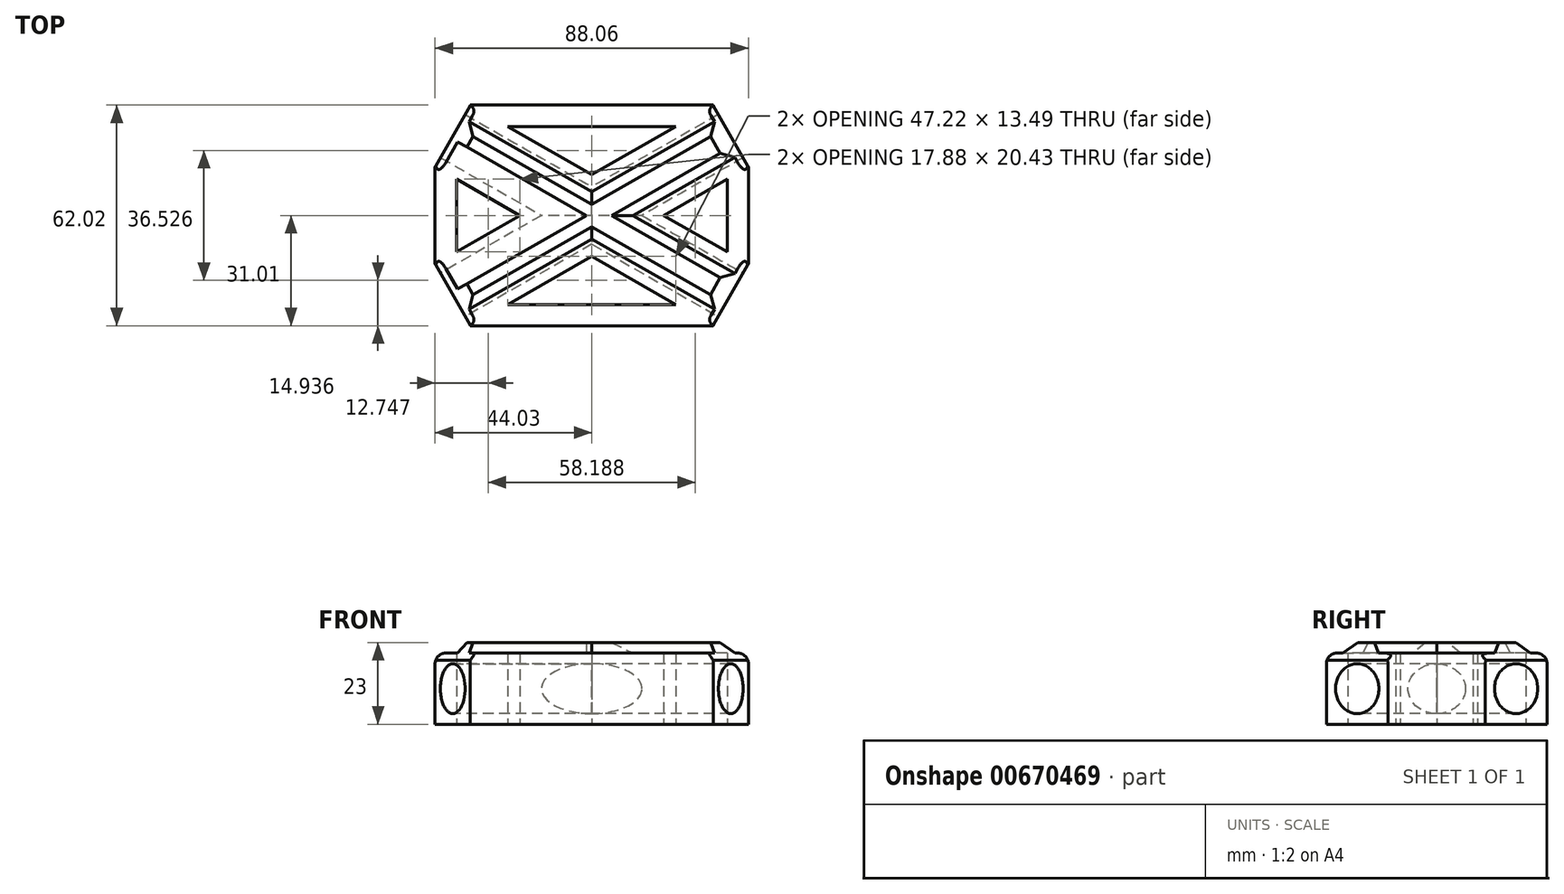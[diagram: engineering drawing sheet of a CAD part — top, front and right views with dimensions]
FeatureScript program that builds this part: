
annotation { "Feature Type Name" : "Feature", "Feature Type Description" : "" }
export const myFeature = defineFeature(function(context is Context, id is Id, definition is map)
    precondition{}
    {
        {
            var Q0;
            Q0=qCreatedBy(makeId("Top.planeOp"),FACE);
            var sketch = newSketch(context, id + "F0", { "sketchPlane" : qUnion([Q0])});
            skPoint(sketch, "E0.middle", {"position": v(0, 0) * mm});
            skLineSegment(sketch, "E1.bottom", {"start": v(70, 40) * mm, "end": v(-70, 40) * mm, "construction": true});
            skLineSegment(sketch, "E1.top", {"start": v(70, -40) * mm, "end": v(-70, -40) * mm, "construction": true});
            skLineSegment(sketch, "E1.left", {"start": v(70, 40) * mm, "end": v(70, -40) * mm, "construction": true});
            skLineSegment(sketch, "E1.right", {"start": v(-70, 40) * mm, "end": v(-70, -40) * mm, "construction": true});
            skLineSegment(sketch, "E2", {"start": v(-70, 40) * mm, "end": v(70, -40) * mm, "construction": true});
            skLineSegment(sketch, "E3", {"start": v(70, 40) * mm, "end": v(-70, -40) * mm, "construction": true});
            skPoint(sketch, "E4", {"position": v(-34.1, 31) * mm});
            skPoint(sketch, "E5", {"position": v(34.1, 31) * mm});
            skPoint(sketch, "E6", {"position": v(-34.1, -31) * mm});
            skPoint(sketch, "E7", {"position": v(-44.03, -13.64) * mm});
            skPoint(sketch, "E8", {"position": v(-44.03, 13.64) * mm});
            skPoint(sketch, "E9", {"position": v(34.1, -31) * mm});
            skPoint(sketch, "E10", {"position": v(44.03, -13.64) * mm});
            skPoint(sketch, "E11", {"position": v(44.03, 13.64) * mm});
            skLineSegment(sketch, "E12", {"start": v(-34.1, 31) * mm, "end": v(-34.1, 31) * mm});
            skPoint(sketch, "E13", {"position": v(0, 25) * mm});
            skLineSegment(sketch, "E14", {"start": v(0, 25) * mm, "end": v(-23.6, 25) * mm});
            skLineSegment(sketch, "E15", {"start": v(0, 25) * mm, "end": v(23.6, 25) * mm});
            skLineSegment(sketch, "E16.MirrorCS", {"start": v(0, -25) * mm, "end": v(-23.6, -25) * mm});
            skLineSegment(sketch, "E17.MirrorCS", {"start": v(-34.1, -31) * mm, "end": v(34.1, -31) * mm});
            skLineSegment(sketch, "E18.MirrorCS", {"start": v(0, -25) * mm, "end": v(23.6, -25) * mm});
            skLineSegment(sketch, "E19", {"start": v(44.03, 13.64) * mm, "end": v(44.03, -13.64) * mm});
            skPoint(sketch, "E20", {"position": v(38.03, 0) * mm});
            skLineSegment(sketch, "E21", {"start": v(38.03, 0) * mm, "end": v(38.03, 10.22) * mm});
            skLineSegment(sketch, "E22", {"start": v(38.03, 0) * mm, "end": v(38.03, -10.22) * mm});
            skLineSegment(sketch, "E23.MirrorCS", {"start": v(-38.03, 0) * mm, "end": v(-38.03, 10.22) * mm});
            skLineSegment(sketch, "E24.MirrorCS", {"start": v(-38.03, 0) * mm, "end": v(-38.03, -10.22) * mm});
            skLineSegment(sketch, "E25.MirrorCS", {"start": v(-44.03, 13.64) * mm, "end": v(-44.03, -13.64) * mm});
            skLineSegment(sketch, "E26", {"start": v(-34.1, 31) * mm, "end": v(34.1, 31) * mm});
            skLineSegment(sketch, "E27", {"start": v(-44.03, 13.64) * mm, "end": v(34.1, -31) * mm});
            skLineSegment(sketch, "E28", {"start": v(-44.03, -13.64) * mm, "end": v(-44.03, -13.64) * mm});
            skLineSegment(sketch, "E29", {"start": v(44.03, 13.64) * mm, "end": v(-34.1, -31) * mm});
            skLineSegment(sketch, "E30", {"start": v(34.1, 31) * mm, "end": v(34.1, 31) * mm});
            skLineSegment(sketch, "E31", {"start": v(-34.1, 31) * mm, "end": v(-44.03, 13.64) * mm});
            skLineSegment(sketch, "E32", {"start": v(-44.03, -13.64) * mm, "end": v(-34.1, -31) * mm});
            skLineSegment(sketch, "E33", {"start": v(34.1, -31) * mm, "end": v(44.03, -13.64) * mm});
            skLineSegment(sketch, "E34", {"start": v(44.03, 13.64) * mm, "end": v(34.1, 31) * mm});
            skLineSegment(sketch, "E35", {"start": v(34.1, 31) * mm, "end": v(-44.03, -13.64) * mm});
            skLineSegment(sketch, "E36", {"start": v(-34.1, 31) * mm, "end": v(44.03, -13.64) * mm});
            skSolve(sketch);
        }
        {
            var Q0;
            Q0 = qSketchRegion(id + "F0", true);
            var Q1;
            {var subQ0=sQuery(id+"F0.wireOp",EDGE,"E35");var subQ1=sQuery(id+"F0.wireOp",EDGE,"E27");var subQ2=makeQuery(id+"F0.imprint","INTERSECT",VERTEX,{"derivedFrom":[subQ1,subQ0]});Q1=makeQuery(id+"F0.imprint","IMPRINT",FACE,{"disambiguationData":[TD([[makeQuery(id+"F0.imprint","IMPRINT",EDGE,{"disambiguationData":[TD([[subQ2,-1.0]])],"derivedFrom":subQ1}),1.0]])]});}
            extrude(context, id + "F1", {"entities" : qUnion([Q0, Q1]), "depth" : 20 * mm, "offsetDistance" : 25 * mm});
        }
        {
            var Q0;
            Q0=makeQuery(id+"F1.opExtrude","SWEPT_FACE",FACE,{"disambiguationData":[OSD([sQuery(id+"F0.wireOp",EDGE,"E32")])]});
            var sketch = newSketch(context, id + "F2", { "sketchPlane" : qUnion([Q0])});
            skLineSegment(sketch, "E37.0", {"start": v(-10, 20) * mm, "end": v(10, 20) * mm, "construction": true});
            skLineSegment(sketch, "E38.0", {"start": v(10, 20) * mm, "end": v(10, 0) * mm, "construction": true});
            skLineSegment(sketch, "E39.0", {"start": v(-10, 0) * mm, "end": v(10, 0) * mm, "construction": true});
            skLineSegment(sketch, "E40.0", {"start": v(-10, 20) * mm, "end": v(-10, 0) * mm, "construction": true});
            skLineSegment(sketch, "E41", {"start": v(-10, 20) * mm, "end": v(10, 0) * mm, "construction": true});
            skLineSegment(sketch, "E42", {"start": v(10, 20) * mm, "end": v(-10, 0) * mm, "construction": true});
            skCircle(sketch, "E43", {"center": v(0, 10) * mm, "radius": 7 * mm});
            skSolve(sketch);
        }
        {
            var Q0;
            Q0 = qSketchRegion(id + "F2", true);
            var Q1;
            Q1 = qConstructionFilter(qBodyType(qCreatedBy(id + "F2" ,EDGE), BodyType.WIRE), ConstructionObject.NO);
            extrude(context, id + "F3", {"entities" : qUnion([Q0]), "operationType" : NewBodyOperationType.REMOVE, "surfaceEntities" : qUnion([Q1]), "endBound" : BoundingType.THROUGH_ALL, "oppositeDirection" : true, "depth" : 25 * mm, "offsetDistance" : 25 * mm, "hasSecondDirection" : true, "secondDirectionBound" : SecondDirectionBoundingType.THROUGH_ALL, "secondDirectionOppositeDirection" : false, "secondDirectionDepth" : 25 * mm});
        }
        {
            var Q0;
            Q0=makeQuery(id+"F1.opExtrude","SWEPT_FACE",FACE,{"disambiguationData":[OSD([sQuery(id+"F0.wireOp",EDGE,"E33")])]});
            var sketch = newSketch(context, id + "F4", { "sketchPlane" : qUnion([Q0])});
            skLineSegment(sketch, "E44.0", {"start": v(10, 20) * mm, "end": v(-10, 20) * mm, "construction": true});
            skLineSegment(sketch, "E45.0", {"start": v(10, 20) * mm, "end": v(10, 0) * mm, "construction": true});
            skLineSegment(sketch, "E46.0", {"start": v(10, 0) * mm, "end": v(-10, 0) * mm, "construction": true});
            skLineSegment(sketch, "E47.0", {"start": v(-10, 20) * mm, "end": v(-10, 0) * mm, "construction": true});
            skLineSegment(sketch, "E48", {"start": v(-10, 20) * mm, "end": v(10, 0) * mm, "construction": true});
            skLineSegment(sketch, "E49", {"start": v(10, 20) * mm, "end": v(-10, 0) * mm, "construction": true});
            skCircle(sketch, "E50", {"center": v(0, 10) * mm, "radius": 7 * mm});
            skSolve(sketch);
        }
        {
            var Q0;
            Q0 = qSketchRegion(id + "F4", true);
            extrude(context, id + "F5", {"entities" : qUnion([Q0]), "operationType" : NewBodyOperationType.REMOVE, "endBound" : BoundingType.THROUGH_ALL, "oppositeDirection" : true, "depth" : 25 * mm, "offsetDistance" : 25 * mm, "hasSecondDirection" : true, "secondDirectionBound" : SecondDirectionBoundingType.THROUGH_ALL, "secondDirectionOppositeDirection" : false, "secondDirectionDepth" : 25 * mm});
        }
        {
            var Q0;
            Q0=makeQuery(id+"F1.opExtrude","CAP_FACE",FACE,{"disambiguationData":[OSD([sQuery(id+"F0.wireOp",EDGE,"E14"),sQuery(id+"F0.wireOp",EDGE,"E15"),sQuery(id+"F0.wireOp",EDGE,"E16.MirrorCS"),sQuery(id+"F0.wireOp",EDGE,"E17.MirrorCS"),sQuery(id+"F0.wireOp",EDGE,"E18.MirrorCS"),sQuery(id+"F0.wireOp",EDGE,"E19"),sQuery(id+"F0.wireOp",EDGE,"E21"),sQuery(id+"F0.wireOp",EDGE,"E22"),sQuery(id+"F0.wireOp",EDGE,"E23.MirrorCS"),sQuery(id+"F0.wireOp",EDGE,"E24.MirrorCS"),sQuery(id+"F0.wireOp",EDGE,"E25.MirrorCS"),sQuery(id+"F0.wireOp",EDGE,"E26"),sQuery(id+"F0.wireOp",EDGE,"E27"),sQuery(id+"F0.wireOp",EDGE,"E29"),sQuery(id+"F0.wireOp",EDGE,"E31"),sQuery(id+"F0.wireOp",EDGE,"E32"),sQuery(id+"F0.wireOp",EDGE,"E33"),sQuery(id+"F0.wireOp",EDGE,"E34"),sQuery(id+"F0.wireOp",EDGE,"E35"),sQuery(id+"F0.wireOp",EDGE,"E36")])],"isStart":false});
            var sketch = newSketch(context, id + "F6", { "sketchPlane" : qUnion([Q0])});
            skLineSegment(sketch, "E51.0", {"start": v(70, 40) * mm, "end": v(-70, -40) * mm, "construction": true});
            skLineSegment(sketch, "E52.0", {"start": v(-70, 40) * mm, "end": v(70, -40) * mm, "construction": true});
            skLineSegment(sketch, "E53", {"start": v(-38.7, 22.98) * mm, "end": v(-39.07, 22.33) * mm});
            skLineSegment(sketch, "E54", {"start": v(38.7, 22.98) * mm, "end": v(39.07, 22.33) * mm});
            skLineSegment(sketch, "E55", {"start": v(39.44, -21.68) * mm, "end": v(39.07, -22.33) * mm});
            skLineSegment(sketch, "E56", {"start": v(-39.44, -21.68) * mm, "end": v(-39.07, -22.33) * mm});
            skLineSegment(sketch, "E57.MirrorCS", {"start": v(39.44, 21.68) * mm, "end": v(39.07, 22.33) * mm});
            skLineSegment(sketch, "E58.MirrorCS", {"start": v(-39.44, 21.68) * mm, "end": v(-39.07, 22.33) * mm});
            skLineSegment(sketch, "E59.MirrorCS", {"start": v(-38.7, -22.98) * mm, "end": v(-39.07, -22.33) * mm});
            skLineSegment(sketch, "E60.MirrorCS", {"start": v(38.7, -22.98) * mm, "end": v(39.07, -22.33) * mm});
            skLineSegment(sketch, "E61", {"start": v(-38.7, 22.98) * mm, "end": v(39.44, -21.68) * mm});
            skLineSegment(sketch, "E62", {"start": v(-39.44, 21.68) * mm, "end": v(38.7, -22.98) * mm});
            skLineSegment(sketch, "E63", {"start": v(38.7, 22.98) * mm, "end": v(-39.44, -21.68) * mm});
            skLineSegment(sketch, "E64", {"start": v(39.44, 21.68) * mm, "end": v(-38.7, -22.98) * mm});
            skSolve(sketch);
        }
        {
            var Q0;
            Q0 = qSketchRegion(id + "F6", true);
            extrude(context, id + "F7", {"entities" : qUnion([Q0]), "operationType" : NewBodyOperationType.ADD, "depth" : 3 * mm, "offsetDistance" : 25 * mm});
        }
        {
            var Q0;
            {var subQ0=sQuery(id+"F6.wireOp",EDGE,"E64");Q0=makeQuery(id+"F7.opExtrude","CAP_EDGE",EDGE,{"disambiguationData":[OSD([subQ0]),TDD([makeQuery(id+"F6.imprint","IMPRINT",EDGE,{"disambiguationData":[TD([[makeQuery(id+"F6.imprint","INTERSECT",VERTEX,{"derivedFrom":[sQuery(id+"F6.wireOp",EDGE,"E62"),subQ0]}),-1.0]])],"derivedFrom":subQ0})])],"isStart":true});}
            var Q1;
            {var subQ0=sQuery(id+"F6.wireOp",EDGE,"E62");Q1=makeQuery(id+"F7.opExtrude","CAP_EDGE",EDGE,{"disambiguationData":[OSD([subQ0]),TDD([makeQuery(id+"F6.imprint","IMPRINT",EDGE,{"disambiguationData":[TD([[makeQuery(id+"F6.imprint","INTERSECT",VERTEX,{"derivedFrom":[subQ0,sQuery(id+"F6.wireOp",EDGE,"E64")]}),-1.0]])],"derivedFrom":subQ0})])],"isStart":true});}
            var Q2;
            {var subQ0=sQuery(id+"F6.wireOp",EDGE,"E63");Q2=makeQuery(id+"F7.opExtrude","CAP_EDGE",EDGE,{"disambiguationData":[OSD([subQ0]),TDD([makeQuery(id+"F6.imprint","IMPRINT",EDGE,{"disambiguationData":[TD([[makeQuery(id+"F6.imprint","INTERSECT",VERTEX,{"derivedFrom":[sQuery(id+"F6.wireOp",EDGE,"E62"),subQ0]}),-1.0]])],"derivedFrom":subQ0})])],"isStart":true});}
            var Q3;
            {var subQ0=sQuery(id+"F6.wireOp",EDGE,"E62");Q3=makeQuery(id+"F7.opExtrude","CAP_EDGE",EDGE,{"disambiguationData":[OSD([subQ0]),TDD([makeQuery(id+"F6.imprint","IMPRINT",EDGE,{"disambiguationData":[TD([[makeQuery(id+"F6.imprint","INTERSECT",VERTEX,{"derivedFrom":[subQ0,sQuery(id+"F6.wireOp",EDGE,"E63")]}),1.0]])],"derivedFrom":subQ0})])],"isStart":true});}
            var Q4;
            {var subQ0=sQuery(id+"F6.wireOp",EDGE,"E61");Q4=makeQuery(id+"F7.opExtrude","CAP_EDGE",EDGE,{"disambiguationData":[OSD([subQ0]),TDD([makeQuery(id+"F6.imprint","IMPRINT",EDGE,{"disambiguationData":[TD([[makeQuery(id+"F6.imprint","INTERSECT",VERTEX,{"derivedFrom":[subQ0,sQuery(id+"F6.wireOp",EDGE,"E64")]}),-1.0]])],"derivedFrom":subQ0})])],"isStart":true});}
            var Q5;
            {var subQ0=sQuery(id+"F6.wireOp",EDGE,"E64");Q5=makeQuery(id+"F7.opExtrude","CAP_EDGE",EDGE,{"disambiguationData":[OSD([subQ0]),TDD([makeQuery(id+"F6.imprint","IMPRINT",EDGE,{"disambiguationData":[TD([[makeQuery(id+"F6.imprint","INTERSECT",VERTEX,{"derivedFrom":[sQuery(id+"F6.wireOp",EDGE,"E61"),subQ0]}),1.0]])],"derivedFrom":subQ0})])],"isStart":true});}
            var Q6;
            {var subQ0=sQuery(id+"F6.wireOp",EDGE,"E61");Q6=makeQuery(id+"F7.opExtrude","CAP_EDGE",EDGE,{"disambiguationData":[OSD([subQ0]),TDD([makeQuery(id+"F6.imprint","IMPRINT",EDGE,{"disambiguationData":[TD([[makeQuery(id+"F6.imprint","INTERSECT",VERTEX,{"derivedFrom":[subQ0,sQuery(id+"F6.wireOp",EDGE,"E63")]}),1.0]])],"derivedFrom":subQ0})])],"isStart":true});}
            var Q7;
            {var subQ0=sQuery(id+"F6.wireOp",EDGE,"E63");Q7=makeQuery(id+"F7.opExtrude","CAP_EDGE",EDGE,{"disambiguationData":[OSD([subQ0]),TDD([makeQuery(id+"F6.imprint","IMPRINT",EDGE,{"disambiguationData":[TD([[makeQuery(id+"F6.imprint","INTERSECT",VERTEX,{"derivedFrom":[sQuery(id+"F6.wireOp",EDGE,"E61"),subQ0]}),1.0]])],"derivedFrom":subQ0})])],"isStart":true});}
            chamfer(context, id + "F8", {"entities" : qUnion([Q0, Q1, Q2, Q3, Q4, Q5, Q6, Q7]), "width" : 5 * mm, "tangentPropagation" : true});
        }
        {
            var Q0;
            Q0=makeQuery(id+"F7.opExtrude","CAP_EDGE",EDGE,{"disambiguationData":[OSD([sQuery(id+"F6.wireOp",EDGE,"E56"),sQuery(id+"F6.wireOp",EDGE,"E59.MirrorCS")])],"isStart":false});
            var Q1;
            Q1=makeQuery(id+"F7.opExtrude","CAP_EDGE",EDGE,{"disambiguationData":[OSD([sQuery(id+"F6.wireOp",EDGE,"E53"),sQuery(id+"F6.wireOp",EDGE,"E58.MirrorCS")])],"isStart":false});
            var Q2;
            Q2=makeQuery(id+"F7.opExtrude","CAP_EDGE",EDGE,{"disambiguationData":[OSD([sQuery(id+"F6.wireOp",EDGE,"E55"),sQuery(id+"F6.wireOp",EDGE,"E60.MirrorCS")])],"isStart":false});
            var Q3;
            Q3=makeQuery(id+"F7.opExtrude","CAP_EDGE",EDGE,{"disambiguationData":[OSD([sQuery(id+"F6.wireOp",EDGE,"E54"),sQuery(id+"F6.wireOp",EDGE,"E57.MirrorCS")])],"isStart":false});
            chamfer(context, id + "F9", {"entities" : qUnion([Q0, Q1, Q2, Q3]), "width" : 5 * mm, "tangentPropagation" : true});
        }
        {
            var Q0;
            Q0=makeQuery(id+"F1.opExtrude","CAP_EDGE",EDGE,{"disambiguationData":[OSD([sQuery(id+"F0.wireOp",EDGE,"E26")])],"isStart":false});
            var Q1;
            Q1=makeQuery(id+"F1.opExtrude","CAP_EDGE",EDGE,{"disambiguationData":[OSD([sQuery(id+"F0.wireOp",EDGE,"E17.MirrorCS")])],"isStart":false});
            var Q2;
            Q2=makeQuery(id+"F1.opExtrude","CAP_EDGE",EDGE,{"disambiguationData":[OSD([sQuery(id+"F0.wireOp",EDGE,"E25.MirrorCS")])],"isStart":false});
            var Q3;
            Q3=makeQuery(id+"F1.opExtrude","CAP_EDGE",EDGE,{"disambiguationData":[OSD([sQuery(id+"F0.wireOp",EDGE,"E19")])],"isStart":false});
            fillet(context, id + "F10", {"entities" : qUnion([Q0, Q1, Q2, Q3]), "radius" : 3 * mm, "tangentPropagation" : true, "allowEdgeOverflow" : false});
        }
    });
